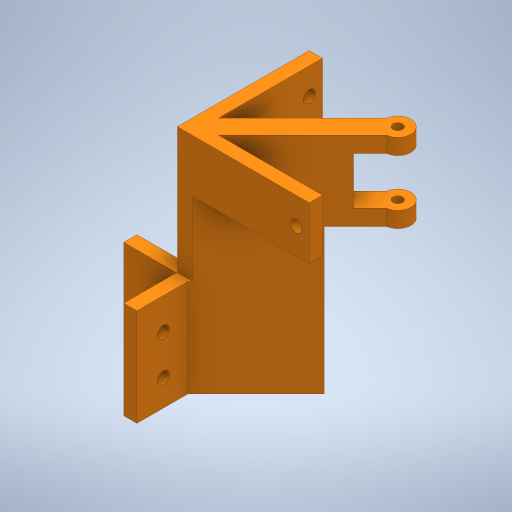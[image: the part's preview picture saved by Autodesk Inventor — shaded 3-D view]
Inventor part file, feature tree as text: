
AUTODESK INVENTOR PART (.ipt)
format: ipt  version: 2023 (Build 270158000, 158)  size: 368,640 bytes
history: native  units: mm
features: extrude x10, sketch x10, projected_geometry x2, plane x1
ambient origin geometry x8: Origin, YZ Plane, XZ Plane, XY Plane, X Axis, Y Axis, Z Axis, Center Point
bodies: Solid1 (feature_tree)
feature tree (23):
  extrude  "Extrusion1"  Depth=20.0mm
  plane  "Work Plane1"
  sketch  "Sketch3"  dims[d2=5.0mm d3=5.0mm]
  extrude  "Extrusion3"  Depth=5.0mm
  extrude  "Extrusion5"  Depth=42.0mm
  sketch  "Sketch8"  dims[d8=42.0mm d9=3.7mm]
  extrude  "Extrusion8"  Depth=42.0mm
  extrude  "Extrusion9"  Depth=25.0mm
  extrude  "Extrusion10"  Depth=5.0mm
  extrude  "Extrusion12"  Depth=55.0mm TaperAngle=0.0deg
  sketch  "Sketch13"  dims[d40=4.5mm d41=10.0mm]
  sketch  "Sketch14"  dims[d42=10.0mm d43=4.5mm]
  extrude  "Extrusion13"  Depth=10.0mm
  extrude  "Extrusion14"  Depth=10.0mm
  extrude  "Extrusion15"  Depth=55.0mm
  sketch  "Sketch1"  dims[d0=20.0mm d1=20.0mm]
  sketch  "Sketch5"  dims[d5=30.0mm d6=0.0mm d7=42.0mm]
  projected_geometry  "Projected Loop2"
  sketch  "Sketch9"  dims[d10=-6.0mm d13=25.0mm]
  sketch  "Sketch10"  dims[d16=18.0mm d17=0.0mm d18=5.0mm]
  sketch  "Sketch12"  dims[d19=135.0deg d22=55.0mm d23=0.0mm]
  sketch  "Sketch15"  dims[d44=10.0mm d45=15.0mm d46=10.0mm d47=10.0mm d48=10.0mm d49=15.0mm d50=4.5mm d51=4.5mm d52=20.0mm d53=0.0mm d54=20.0mm d55=0.0mm d56=135.0deg d58=48.0mm d59=0.0mm d65=0.2mm d66=0.2mm d67=8.0mm d68=5.0mm d70=50.0mm d71=50.0mm d72=20.0mm d73=0.0mm d75=0.0mm d76=5.0mm d77=10.0mm d78=5.0mm d79=4.5mm d80=5.0mm d81=4.5mm d82=10.0mm d83=20.0mm d84=0.0mm d85=20.0mm d86=0.0mm d87=55.0mm d88=0.0mm d63=0.5mm d64=0.872665mm]
  projected_geometry  "Projected Loop3"
